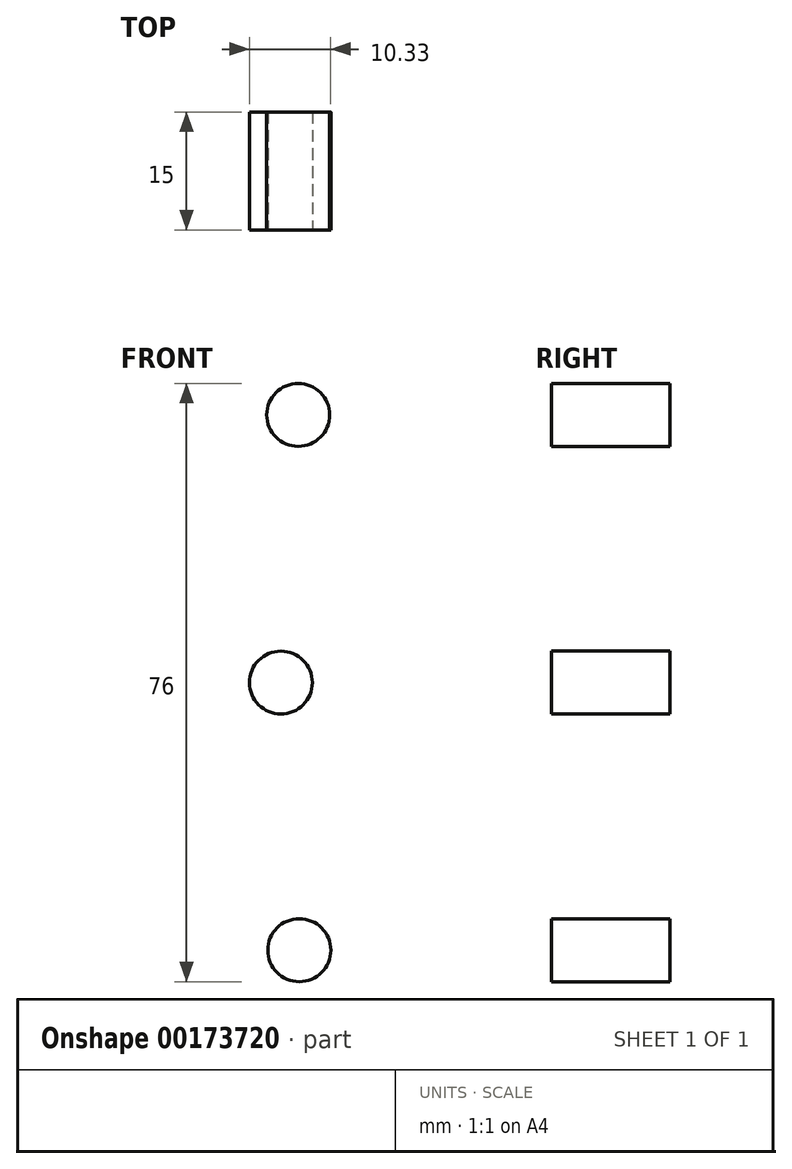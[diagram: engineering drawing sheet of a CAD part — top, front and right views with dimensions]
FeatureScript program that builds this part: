
annotation { "Feature Type Name" : "Feature", "Feature Type Description" : "" }
export const myFeature = defineFeature(function(context is Context, id is Id, definition is map)
    precondition{}
    {
        {
            var Q0;
            Q0=qCreatedBy(makeId("Front.planeOp"),FACE);
            var sketch = newSketch(context, id + "F0", { "sketchPlane" : qUnion([Q0])});
            skLineSegment(sketch, "E0.bottom", {"start": v(40, 62.5) * mm, "end": v(-40, 62.5) * mm});
            skLineSegment(sketch, "E0.top", {"start": v(40, -62.5) * mm, "end": v(-40, -62.5) * mm});
            skLineSegment(sketch, "E0.left", {"start": v(40, 62.5) * mm, "end": v(40, -62.5) * mm});
            skLineSegment(sketch, "E0.right", {"start": v(-40, 62.5) * mm, "end": v(-40, -62.5) * mm});
            skPoint(sketch, "E0.middle", {"position": v(0, 0) * mm});
            skArc(sketch, "E1", {"start": v(-40, -62.5) * mm, "mid": v(-31.76, 0) * mm, "end": v(-40, 62.5) * mm});
            skArc(sketch, "E2.MirrorCS", {"start": v(40, -62.5) * mm, "mid": v(31.76, 0) * mm, "end": v(40, 62.5) * mm});
            skArc(sketch, "E3", {"start": v(40, 62.5) * mm, "mid": v(0, 87.5) * mm, "end": v(-40, 62.5) * mm});
            skSolve(sketch);
        }
        {
            var Q0;
            Q0=makeQuery(id+"F0.imprint","IMPRINT",FACE,{"disambiguationData":[TD([[makeQuery(id+"F0.imprint","IMPRINT",EDGE,{"derivedFrom":sQuery(id+"F0.wireOp",EDGE,"E0.bottom")}),1.0]])]});
            var Q1;
            Q1=makeQuery(id+"F0.imprint","IMPRINT",FACE,{"disambiguationData":[TD([[makeQuery(id+"F0.imprint","IMPRINT",EDGE,{"derivedFrom":sQuery(id+"F0.wireOp",EDGE,"E0.bottom")}),-1.0]])]});
            extrude(context, id + "F1", {"entities" : qUnion([Q0, Q1]), "depth" : 15 * mm});
        }
        {
            var Q0;
            Q0=makeQuery(id+"F1.opExtrude","CAP_FACE",FACE,{"disambiguationData":[OSD([sQuery(id+"F0.wireOp",EDGE,"E0.top"),sQuery(id+"F0.wireOp",EDGE,"E1"),sQuery(id+"F0.wireOp",EDGE,"E2.MirrorCS"),sQuery(id+"F0.wireOp",EDGE,"E3")])],"isStart":false});
            var sketch = newSketch(context, id + "F2", { "sketchPlane" : qUnion([Q0])});
            skCircle(sketch, "E4", {"center": v(-19.1, -34.5) * mm, "radius": 4 * mm});
            skCircle(sketch, "E5", {"center": v(-16.76, -0.5) * mm, "radius": 4 * mm});
            skCircle(sketch, "E6", {"center": v(-18.96, 33.5) * mm, "radius": 4 * mm});
            skCircle(sketch, "E7.MirrorC", {"center": v(18.96, 33.5) * mm, "radius": 4 * mm});
            skCircle(sketch, "E8.MirrorC", {"center": v(16.76, -0.5) * mm, "radius": 4 * mm});
            skCircle(sketch, "E9.MirrorC", {"center": v(19.1, -34.5) * mm, "radius": 4 * mm});
            skSolve(sketch);
        }
        {
            var Q0;
            Q0=makeQuery(id+"F2.imprint","IMPRINT",FACE,{"disambiguationData":[TD([[makeQuery(id+"F2.imprint","IMPRINT",EDGE,{"derivedFrom":sQuery(id+"F2.wireOp",EDGE,"E4")}),1.0]])]});
            var Q1;
            Q1=makeQuery(id+"F2.imprint","IMPRINT",FACE,{"disambiguationData":[TD([[makeQuery(id+"F2.imprint","IMPRINT",EDGE,{"derivedFrom":sQuery(id+"F2.wireOp",EDGE,"E5")}),1.0]])]});
            var Q2;
            Q2=makeQuery(id+"F2.imprint","IMPRINT",FACE,{"disambiguationData":[TD([[makeQuery(id+"F2.imprint","IMPRINT",EDGE,{"derivedFrom":sQuery(id+"F2.wireOp",EDGE,"E6")}),1.0]])]});
            var Q3;
            Q3=makeQuery(id+"F2.imprint","IMPRINT",FACE,{"disambiguationData":[TD([[makeQuery(id+"F2.imprint","IMPRINT",EDGE,{"derivedFrom":sQuery(id+"F2.wireOp",EDGE,"E7.MirrorC")}),-1.0]])]});
            var Q4;
            Q4=makeQuery(id+"F2.imprint","IMPRINT",FACE,{"disambiguationData":[TD([[makeQuery(id+"F2.imprint","IMPRINT",EDGE,{"derivedFrom":sQuery(id+"F2.wireOp",EDGE,"E8.MirrorC")}),-1.0]])]});
            var Q5;
            Q5=makeQuery(id+"F2.imprint","IMPRINT",FACE,{"disambiguationData":[TD([[makeQuery(id+"F2.imprint","IMPRINT",EDGE,{"derivedFrom":sQuery(id+"F2.wireOp",EDGE,"E9.MirrorC")}),-1.0]])]});
            extrude(context, id + "F3", {"entities" : qUnion([Q0, Q1, Q2, Q3, Q4, Q5]), "operationType" : NewBodyOperationType.REMOVE, "endBound" : BoundingType.THROUGH_ALL, "oppositeDirection" : true, "depth" : 25 * mm});
        }
    });
